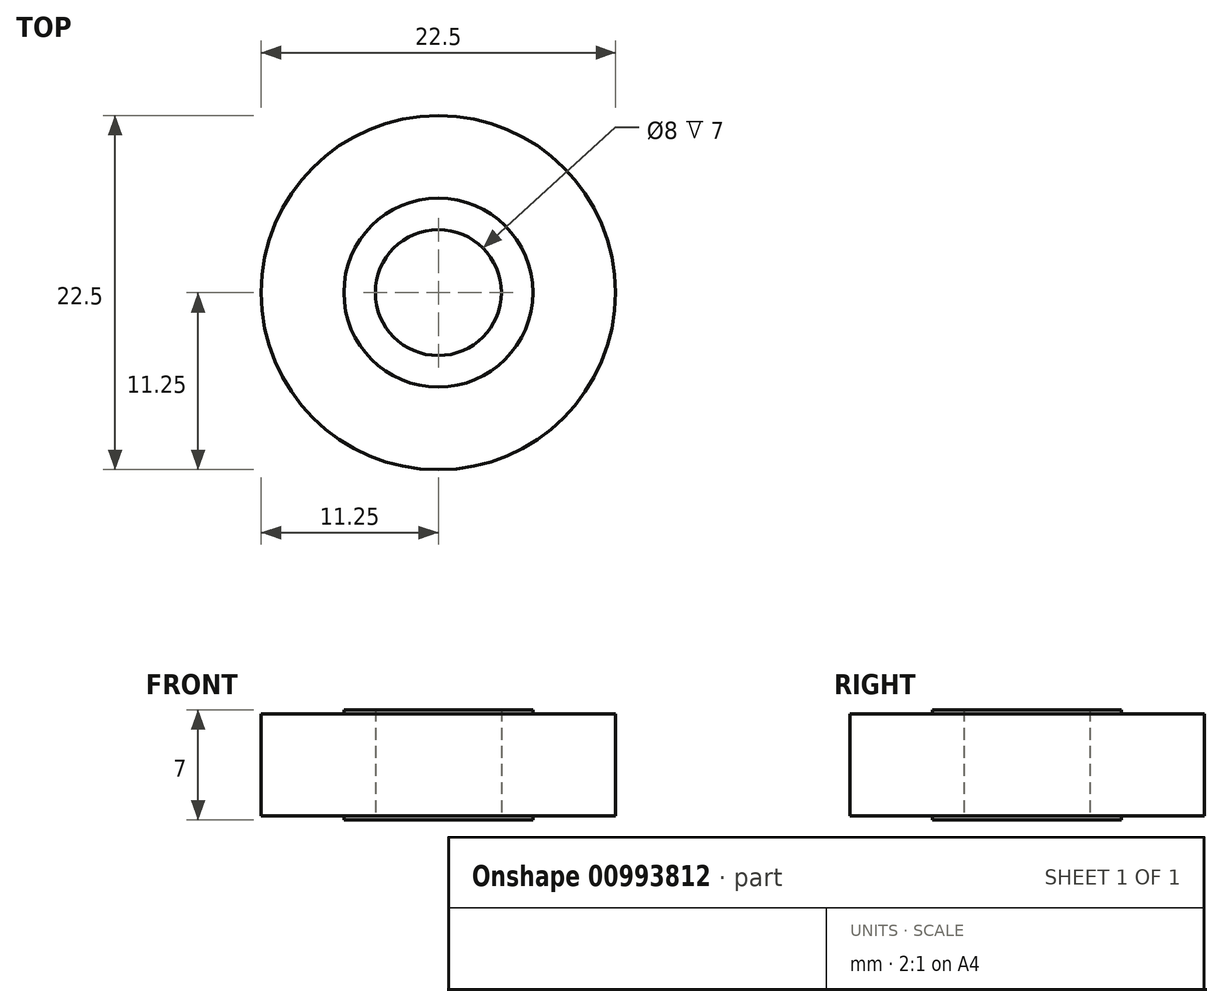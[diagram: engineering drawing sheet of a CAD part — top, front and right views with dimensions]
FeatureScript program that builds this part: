
annotation { "Feature Type Name" : "Feature", "Feature Type Description" : "" }
export const myFeature = defineFeature(function(context is Context, id is Id, definition is map)
    precondition{}
    {
        {
            var Q0;
            Q0=qCreatedBy(makeId("Top.planeOp"),FACE);
            var sketch = newSketch(context, id + "F0", { "sketchPlane" : qUnion([Q0])});
            skCircle(sketch, "E0", {"center": v(0, 0) * mm, "radius": 11.25 * mm});
            skCircle(sketch, "E1", {"center": v(0, 0) * mm, "radius": 4 * mm});
            skCircle(sketch, "E2", {"center": v(0, 0) * mm, "radius": 6 * mm});
            skSolve(sketch);
        }
        {
            var Q0;
            Q0=makeQuery(id+"F0.imprint","IMPRINT",FACE,{"disambiguationData":[TD([[makeQuery(id+"F0.imprint","IMPRINT",EDGE,{"derivedFrom":sQuery(id+"F0.wireOp",EDGE,"E1")}),-1.0]])]});
            extrude(context, id + "F1", {"entities" : qUnion([Q0]), "depth" : 7 * mm, "offsetDistance" : 25 * mm, "symmetric" : true});
        }
        {
            var Q0;
            Q0=makeQuery(id+"F0.imprint","IMPRINT",FACE,{"disambiguationData":[TD([[makeQuery(id+"F0.imprint","IMPRINT",EDGE,{"derivedFrom":sQuery(id+"F0.wireOp",EDGE,"E0")}),1.0]])]});
            extrude(context, id + "F2", {"entities" : qUnion([Q0]), "operationType" : NewBodyOperationType.ADD, "depth" : 6.5 * mm, "offsetDistance" : 25 * mm, "symmetric" : true});
        }
    });
